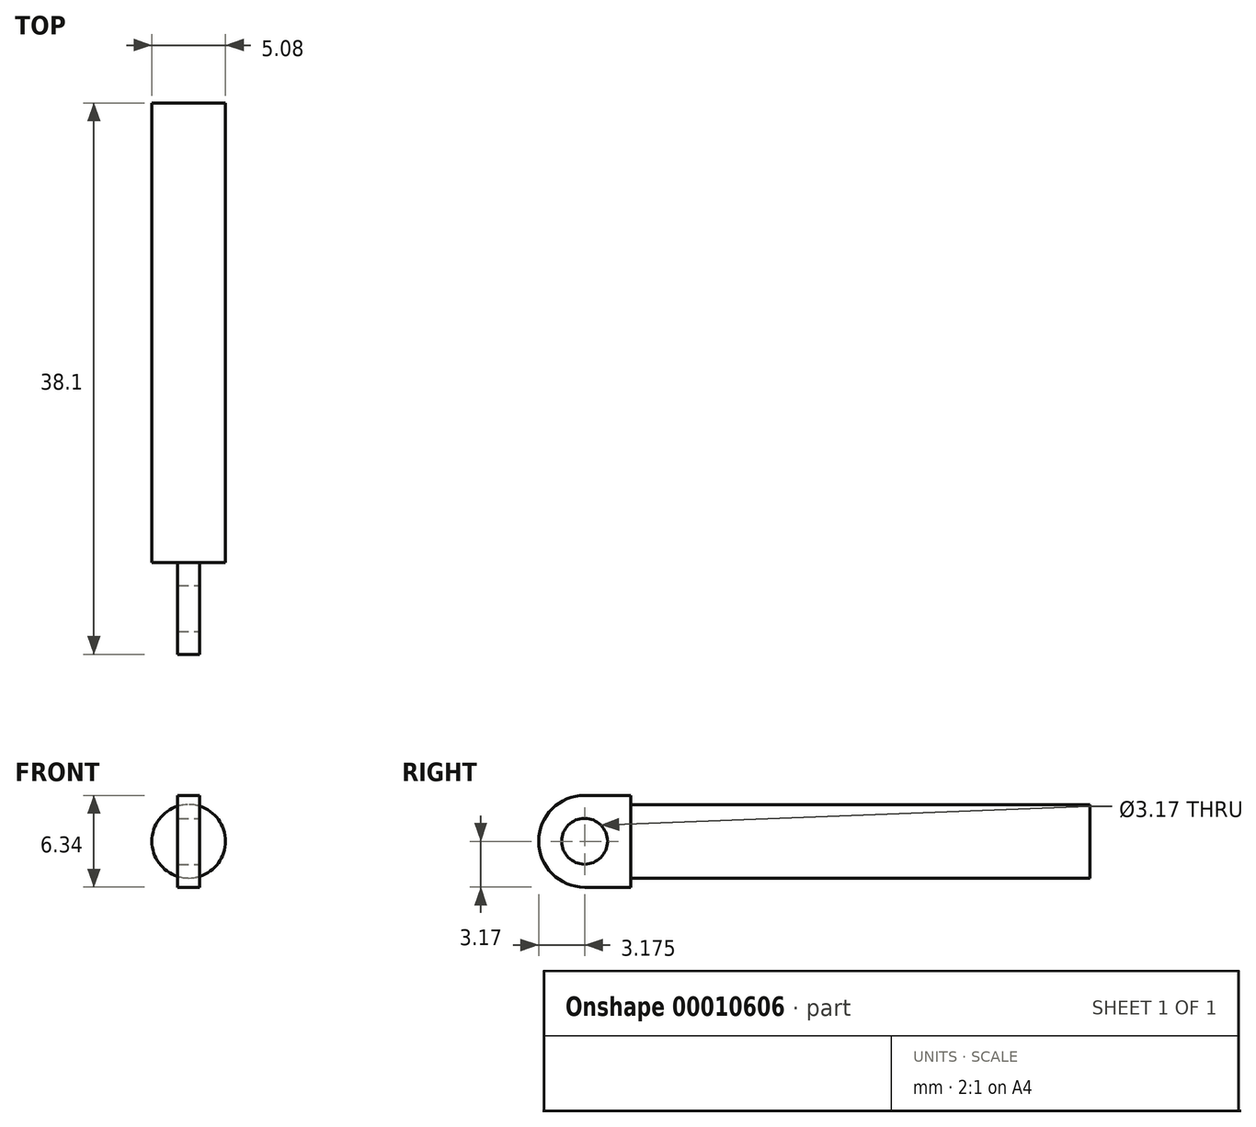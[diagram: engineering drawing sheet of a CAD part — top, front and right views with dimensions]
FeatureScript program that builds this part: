
annotation { "Feature Type Name" : "Feature", "Feature Type Description" : "" }
export const myFeature = defineFeature(function(context is Context, id is Id, definition is map)
    precondition{}
    {
        {
            var Q0;
            Q0=qCreatedBy(makeId("Front.planeOp"),FACE);
            var sketch = newSketch(context, id + "F0", { "sketchPlane" : qUnion([Q0])});
            skCircle(sketch, "E0", {"center": v(0, 0) * mm, "radius": 2.54 * mm});
            skSolve(sketch);
        }
        {
            var Q0;
            Q0=qSketchRegion(id+"F0",true);
            extrude(context, id + "F1", {"entities" : qUnion([Q0]), "depth" : 31.75 * mm});
        }
        {
            var Q0;
            Q0=makeQuery(id+"F1.opExtrude","CAP_FACE",FACE,{"disambiguationData":[OSD([sQuery(id+"F0.wireOp",EDGE,"E0")])],"isStart":false});
            var sketch = newSketch(context, id + "F2", { "sketchPlane" : qUnion([Q0])});
            skCircle(sketch, "E1.0", {"center": v(0, 0) * mm, "radius": 2.54 * mm, "construction": true});
            skLineSegment(sketch, "E2.rect.bottom", {"start": v(0.76, -3.18) * mm, "end": v(-0.76, -3.18) * mm});
            skLineSegment(sketch, "E2.rect.top", {"start": v(0.76, 3.18) * mm, "end": v(-0.76, 3.18) * mm});
            skLineSegment(sketch, "E2.rect.left", {"start": v(0.76, -3.18) * mm, "end": v(0.76, 3.18) * mm});
            skLineSegment(sketch, "E2.rect.right", {"start": v(-0.76, -3.18) * mm, "end": v(-0.76, 3.18) * mm});
            skSolve(sketch);
        }
        {
            var Q0;
            Q0=qSketchRegion(id+"F2",true);
            extrude(context, id + "F3", {"entities" : qUnion([Q0]), "operationType" : NewBodyOperationType.ADD, "depth" : 6.35 * mm});
        }
        {
            var Q0;
            Q0=makeQuery(id+"F3.opExtrude","CAP_EDGE",EDGE,{"disambiguationData":[OSD([sQuery(id+"F2.wireOp",EDGE,"E2.rect.top")])],"isStart":false});
            var Q1;
            Q1=makeQuery(id+"F3.opExtrude","CAP_EDGE",EDGE,{"disambiguationData":[OSD([sQuery(id+"F2.wireOp",EDGE,"E2.rect.bottom")])],"isStart":false});
            fillet(context, id + "F4", {"entities" : qUnion([Q0, Q1]), "radius" : 3.17 * mm, "tangentPropagation" : true, "allowEdgeOverflow" : false});
        }
        {
            var Q0;
            Q0=makeQuery(id+"F3.opExtrude","SWEPT_FACE",FACE,{"disambiguationData":[OSD([sQuery(id+"F2.wireOp",EDGE,"E2.rect.left")])]});
            var sketch = newSketch(context, id + "F5", { "sketchPlane" : qUnion([Q0])});
            skCircle(sketch, "E3", {"center": v(-34.92, 0) * mm, "radius": 1.59 * mm});
            skSolve(sketch);
        }
        {
            var Q0;
            Q0=qSketchRegion(id+"F5",true);
            extrude(context, id + "F6", {"entities" : qUnion([Q0]), "operationType" : NewBodyOperationType.REMOVE, "endBound" : BoundingType.THROUGH_ALL, "oppositeDirection" : true, "depth" : 25.4 * mm});
        }
    });
